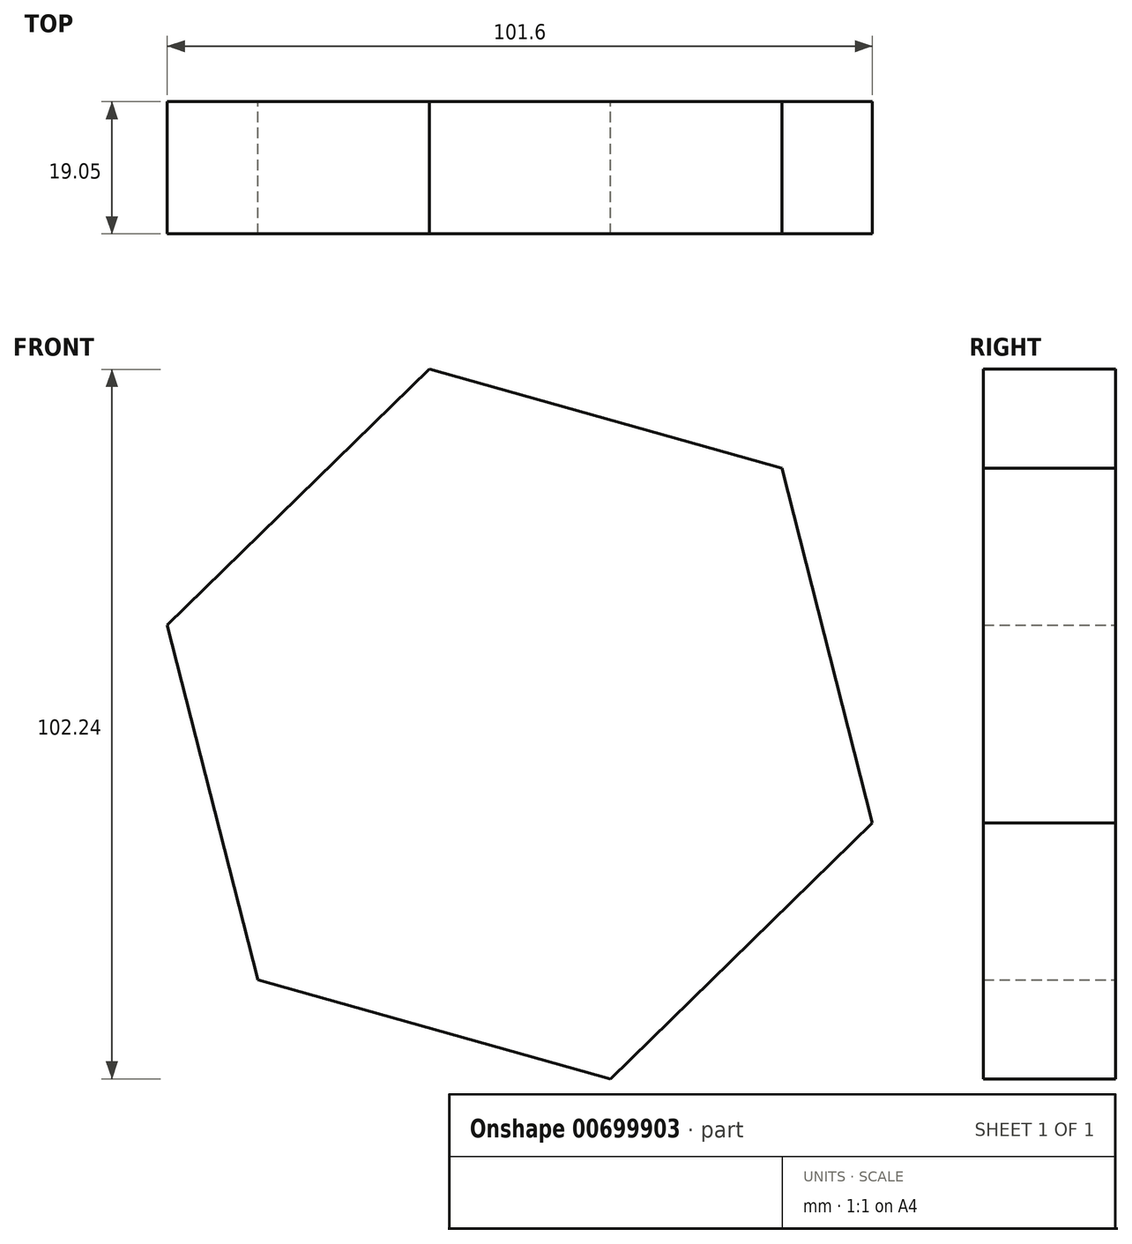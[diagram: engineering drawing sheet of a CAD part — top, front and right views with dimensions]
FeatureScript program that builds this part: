
annotation { "Feature Type Name" : "Feature", "Feature Type Description" : "" }
export const myFeature = defineFeature(function(context is Context, id is Id, definition is map)
    precondition{}
    {
        {
            var Q0;
            Q0=qCreatedBy(makeId("Front.planeOp"),FACE);
            var sketch = newSketch(context, id + "F0", { "sketchPlane" : qUnion([Q0])});
            skCircle(sketch, "E0.cCircle", {"center": v(0, 0) * mm, "radius": 45.7 * mm, "construction": true});
            skLineSegment(sketch, "E0.0", {"start": v(37.75, 36.86) * mm, "end": v(50.8, -14.26) * mm});
            skLineSegment(sketch, "E0.1", {"start": v(50.8, -14.26) * mm, "end": v(13.05, -51.12) * mm});
            skLineSegment(sketch, "E0.2", {"start": v(13.05, -51.12) * mm, "end": v(-37.75, -36.86) * mm});
            skLineSegment(sketch, "E0.3", {"start": v(-37.75, -36.86) * mm, "end": v(-50.8, 14.26) * mm});
            skLineSegment(sketch, "E0.4", {"start": v(-50.8, 14.26) * mm, "end": v(-13.05, 51.12) * mm});
            skLineSegment(sketch, "E0.5", {"start": v(-13.05, 51.12) * mm, "end": v(37.75, 36.86) * mm});
            skPoint(sketch, "E0.0.midPoint", {"position": v(44.27, 11.3) * mm});
            skSolve(sketch);
        }
        {
            var Q0;
            Q0=makeQuery(id+"F0.imprint","IMPRINT",FACE,{"disambiguationData":[TD([[makeQuery(id+"F0.imprint","IMPRINT",EDGE,{"derivedFrom":sQuery(id+"F0.wireOp",EDGE,"E0.0")}),-1.0]])]});
            extrude(context, id + "F1", {"entities" : qUnion([Q0]), "depth" : 19.05 * mm, "offsetDistance" : 25.4 * mm});
        }
    });
